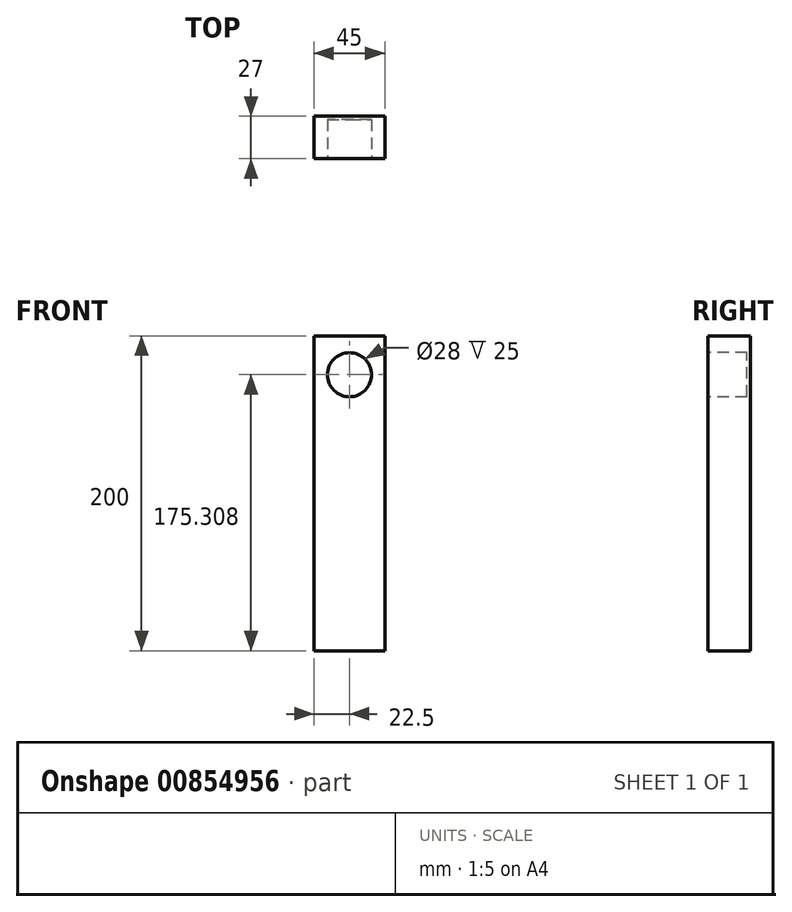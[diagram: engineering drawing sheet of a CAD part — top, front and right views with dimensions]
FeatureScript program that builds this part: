
annotation { "Feature Type Name" : "Feature", "Feature Type Description" : "" }
export const myFeature = defineFeature(function(context is Context, id is Id, definition is map)
    precondition{}
    {
        {
            var Q0;
            Q0=qCreatedBy(makeId("Top.planeOp"),FACE);
            var sketch = newSketch(context, id + "F0", { "sketchPlane" : qUnion([Q0])});
            skLineSegment(sketch, "E0.bottom", {"start": v(22.5, -13.5) * mm, "end": v(-22.5, -13.5) * mm});
            skLineSegment(sketch, "E0.top", {"start": v(22.5, 13.5) * mm, "end": v(-22.5, 13.5) * mm});
            skLineSegment(sketch, "E0.left", {"start": v(22.5, -13.5) * mm, "end": v(22.5, 13.5) * mm});
            skLineSegment(sketch, "E0.right", {"start": v(-22.5, -13.5) * mm, "end": v(-22.5, 13.5) * mm});
            skPoint(sketch, "E0.middle", {"position": v(0, 0) * mm});
            skSolve(sketch);
        }
        {
            var Q0;
            Q0=makeQuery(id+"F0.imprint","IMPRINT",FACE,{"disambiguationData":[TD([[makeQuery(id+"F0.imprint","IMPRINT",EDGE,{"derivedFrom":sQuery(id+"F0.wireOp",EDGE,"E0.bottom")}),-1.0]])]});
            extrude(context, id + "F1", {"entities" : qUnion([Q0]), "depth" : 200 * mm, "offsetDistance" : 25 * mm});
        }
        {
            var Q0;
            Q0=makeQuery(id+"F1.opExtrude","SWEPT_FACE",FACE,{"disambiguationData":[OSD([sQuery(id+"F0.wireOp",EDGE,"E0.bottom")])]});
            var sketch = newSketch(context, id + "F2", { "sketchPlane" : qUnion([Q0])});
            skCircle(sketch, "E1", {"center": v(0, 175.3) * mm, "radius": 14 * mm});
            skSolve(sketch);
        }
        {
            var Q0;
            Q0 = qSketchRegion(id + "F2", true);
            extrude(context, id + "F3", {"entities" : qUnion([Q0]), "operationType" : NewBodyOperationType.REMOVE, "oppositeDirection" : true, "depth" : 25 * mm, "offsetDistance" : 25 * mm});
        }
    });
